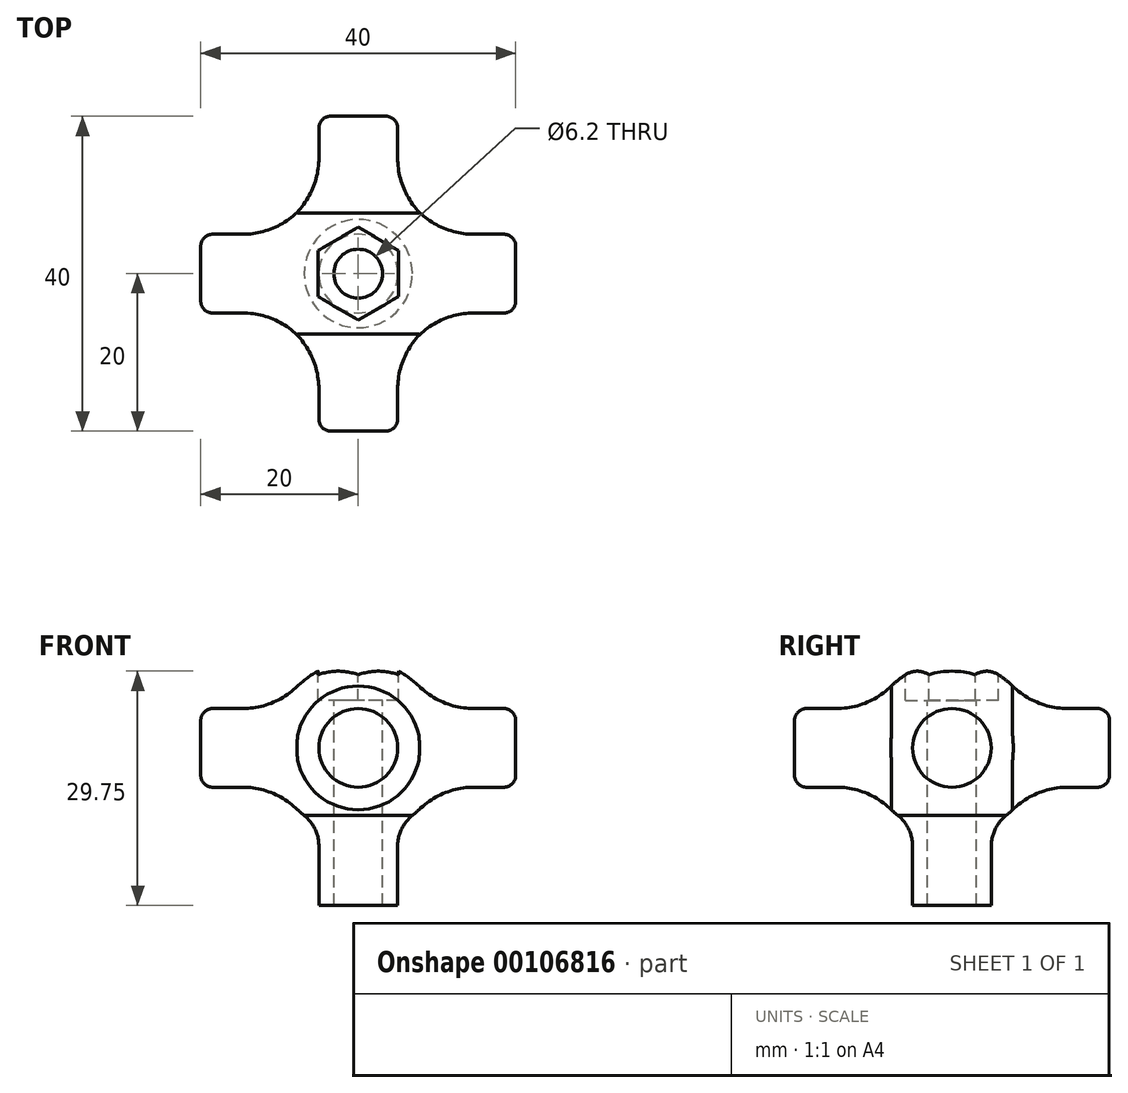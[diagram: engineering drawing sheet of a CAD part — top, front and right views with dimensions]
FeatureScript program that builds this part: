
annotation { "Feature Type Name" : "Feature", "Feature Type Description" : "" }
export const myFeature = defineFeature(function(context is Context, id is Id, definition is map)
    precondition{}
    {
        {
            var Q0;
            Q0=qCreatedBy(makeId("Top.planeOp"),FACE);
            var sketch = newSketch(context, id + "F0", { "sketchPlane" : qUnion([Q0])});
            skCircle(sketch, "E0", {"center": v(0, 0) * mm, "radius": 11 * mm});
            skLineSegment(sketch, "E1", {"start": v(-15.58, 0) * mm, "end": v(16.15, 0) * mm});
            skSolve(sketch);
        }
        {
            var Q0;
            {var subQ0=sQuery(id+"F0.wireOp",EDGE,"E1");var subQ1=sQuery(id+"F0.wireOp",EDGE,"E0");var subQ2=makeQuery(id+"F0.imprint","INTERSECT",VERTEX,{"disambiguationData":[OD(0.0)],"derivedFrom":[subQ1,subQ0]});Q0=makeQuery(id+"F0.imprint","IMPRINT",FACE,{"disambiguationData":[TD([[makeQuery(id+"F0.imprint","IMPRINT",EDGE,{"disambiguationData":[TD([[subQ2,1.0]])],"derivedFrom":subQ1}),1.0]])]});}
            var Q1;
            Q1=sQuery(id+"F0.wireOp",EDGE,"E1");
            revolve(context, id + "F1", {"entities" : qUnion([Q0]), "axis" : qUnion([Q1]), "revolveType" : RevolveType.FULL});
        }
        {
            var Q0;
            Q0=qCreatedBy(makeId("Top.planeOp"),FACE);
            var sketch = newSketch(context, id + "F2", { "sketchPlane" : qUnion([Q0])});
            skCircle(sketch, "E2", {"center": v(0, 0) * mm, "radius": 5 * mm});
            skSolve(sketch);
        }
        {
            var Q0;
            Q0=makeQuery(id+"F2.imprint","IMPRINT",FACE,{"disambiguationData":[TD([[makeQuery(id+"F2.imprint","IMPRINT",EDGE,{"derivedFrom":sQuery(id+"F2.wireOp",EDGE,"E2")}),1.0]])]});
            extrude(context, id + "F3", {"entities" : qUnion([Q0]), "operationType" : NewBodyOperationType.ADD, "oppositeDirection" : true, "depth" : 20 * mm});
        }
        {
            var Q0;
            Q0=qCreatedBy(makeId("Front.planeOp"),FACE);
            var sketch = newSketch(context, id + "F4", { "sketchPlane" : qUnion([Q0])});
            skCircle(sketch, "E3", {"center": v(0, 0) * mm, "radius": 5 * mm});
            skSolve(sketch);
        }
        {
            var Q0;
            Q0=makeQuery(id+"F4.imprint","IMPRINT",FACE,{"disambiguationData":[TD([[makeQuery(id+"F4.imprint","IMPRINT",EDGE,{"derivedFrom":sQuery(id+"F4.wireOp",EDGE,"E3")}),1.0]])]});
            extrude(context, id + "F5", {"entities" : qUnion([Q0]), "operationType" : NewBodyOperationType.ADD, "endBound" : BoundingType.SYMMETRIC, "depth" : 40 * mm});
        }
        {
            var Q0;
            Q0=qCreatedBy(makeId("Right.planeOp"),FACE);
            var sketch = newSketch(context, id + "F6", { "sketchPlane" : qUnion([Q0])});
            skCircle(sketch, "E4", {"center": v(0, 0) * mm, "radius": 5 * mm});
            skSolve(sketch);
        }
        {
            var Q0;
            Q0=makeQuery(id+"F6.imprint","IMPRINT",FACE,{"disambiguationData":[TD([[makeQuery(id+"F6.imprint","IMPRINT",EDGE,{"derivedFrom":sQuery(id+"F6.wireOp",EDGE,"E4")}),1.0]])]});
            extrude(context, id + "F7", {"entities" : qUnion([Q0]), "operationType" : NewBodyOperationType.ADD, "endBound" : BoundingType.SYMMETRIC, "depth" : 40 * mm});
        }
        {
            var Q0;
            Q0=qCreatedBy(makeId("Top.planeOp"),FACE);
            var sketch = newSketch(context, id + "F8", { "sketchPlane" : qUnion([Q0])});
            skLineSegment(sketch, "E5.bottom", {"start": v(-62.48, 40.7) * mm, "end": v(-53.7, 40.7) * mm});
            skLineSegment(sketch, "E5.top", {"start": v(-62.48, 52.9) * mm, "end": v(-53.7, 52.9) * mm});
            skLineSegment(sketch, "E5.left", {"start": v(-62.48, 40.7) * mm, "end": v(-62.48, 52.9) * mm});
            skLineSegment(sketch, "E5.right", {"start": v(-53.7, 40.7) * mm, "end": v(-53.7, 52.9) * mm});
            skSolve(sketch);
        }
        {
            var Q0;
            Q0=makeQuery(id+"F8.imprint","IMPRINT",FACE,{"disambiguationData":[TD([[makeQuery(id+"F8.imprint","IMPRINT",EDGE,{"derivedFrom":sQuery(id+"F8.wireOp",EDGE,"E5.bottom")}),1.0]])]});
            extrude(context, id + "F9", {"entities" : qUnion([Q0]), "depth" : 25 * mm});
        }
        {
            var Q0;
            Q0=makeQuery(id+"F9.opExtrude","CAP_FACE",FACE,{"disambiguationData":[OSD([sQuery(id+"F8.wireOp",EDGE,"E5.bottom"),sQuery(id+"F8.wireOp",EDGE,"E5.top"),sQuery(id+"F8.wireOp",EDGE,"E5.left"),sQuery(id+"F8.wireOp",EDGE,"E5.right")])],"isStart":false});
            var sketch = newSketch(context, id + "F10", { "sketchPlane" : qUnion([Q0])});
            skPoint(sketch, "E6.0", {"position": v(0, 0) * mm});
            skCircle(sketch, "E7.cCircle", {"center": v(0, 0) * mm, "radius": 5.1 * mm, "construction": true});
            skLineSegment(sketch, "E7.0", {"start": v(-5.1, -2.94) * mm, "end": v(-5.1, 2.94) * mm});
            skLineSegment(sketch, "E7.1", {"start": v(-5.1, 2.94) * mm, "end": v(0, 5.89) * mm});
            skLineSegment(sketch, "E7.2", {"start": v(0, 5.89) * mm, "end": v(5.1, 2.94) * mm});
            skLineSegment(sketch, "E7.3", {"start": v(5.1, 2.94) * mm, "end": v(5.1, -2.94) * mm});
            skLineSegment(sketch, "E7.4", {"start": v(5.1, -2.94) * mm, "end": v(0, -5.89) * mm});
            skLineSegment(sketch, "E7.5", {"start": v(0, -5.89) * mm, "end": v(-5.1, -2.94) * mm});
            skPoint(sketch, "E7.0.midPoint", {"position": v(-5.1, 0) * mm});
            skSolve(sketch);
        }
        {
            var Q0;
            Q0=makeQuery(id+"F10.imprint","IMPRINT",FACE,{"disambiguationData":[TD([[makeQuery(id+"F10.imprint","IMPRINT",EDGE,{"derivedFrom":sQuery(id+"F10.wireOp",EDGE,"E7.0")}),-1.0]])]});
            extrude(context, id + "F11", {"entities" : qUnion([Q0]), "operationType" : NewBodyOperationType.REMOVE, "oppositeDirection" : true, "depth" : 19 * mm});
        }
        {
            var Q0;
            Q0=makeQuery(id+"F11.boolean.opBoolean","COPY",FACE,{"derivedFrom":makeQuery(id+"F11.opExtrude","CAP_FACE",FACE,{"disambiguationData":[OSD([sQuery(id+"F10.wireOp",EDGE,"E7.0"),sQuery(id+"F10.wireOp",EDGE,"E7.1"),sQuery(id+"F10.wireOp",EDGE,"E7.2"),sQuery(id+"F10.wireOp",EDGE,"E7.3"),sQuery(id+"F10.wireOp",EDGE,"E7.4"),sQuery(id+"F10.wireOp",EDGE,"E7.5")])],"isStart":false})});
            var sketch = newSketch(context, id + "F12", { "sketchPlane" : qUnion([Q0])});
            skPoint(sketch, "E8.0", {"position": v(0, 0) * mm});
            skCircle(sketch, "E9", {"center": v(0, 0) * mm, "radius": 3.1 * mm});
            skSolve(sketch);
        }
        {
            var Q0;
            Q0=makeQuery(id+"F12.imprint","IMPRINT",FACE,{"disambiguationData":[TD([[makeQuery(id+"F12.imprint","IMPRINT",EDGE,{"derivedFrom":sQuery(id+"F12.wireOp",EDGE,"E9")}),1.0]])]});
            extrude(context, id + "F13", {"entities" : qUnion([Q0]), "operationType" : NewBodyOperationType.REMOVE, "oppositeDirection" : true, "depth" : 43.5 * mm});
        }
        {
            var Q0;
            Q0=makeQuery(id+"F9.opExtrude","SWEPT_BODY",BODY,{"disambiguationData":[OSD([sQuery(id+"F8.wireOp",EDGE,"E5.bottom"),sQuery(id+"F8.wireOp",EDGE,"E5.top"),sQuery(id+"F8.wireOp",EDGE,"E5.left"),sQuery(id+"F8.wireOp",EDGE,"E5.right")])]});
            deleteBodies(context, id + "F14", {"entities" : qUnion([Q0])});
        }
        {
            var Q0;
            Q0=makeQuery(id+"F3.boolean.opBoolean","INTERSECT",EDGE,{"derivedFrom":[makeQuery(id+"F1.opRevolve","SWEPT_FACE",FACE,{"disambiguationData":[OSD([sQuery(id+"F0.wireOp",EDGE,"E0")])]}),makeQuery(id+"F3.opExtrude","SWEPT_FACE",FACE,{"disambiguationData":[OSD([sQuery(id+"F2.wireOp",EDGE,"E2")])]})]});
            fillet(context, id + "F15", {"entities" : qUnion([Q0]), "radius" : 5 * mm, "tangentPropagation" : true, "allowEdgeOverflow" : false});
        }
        {
            var Q0;
            Q0=makeQuery(id+"F7.boolean.opBoolean","INTERSECT",EDGE,{"disambiguationData":[OD(1.0)],"derivedFrom":[makeQuery(id+"F1.opRevolve","SWEPT_FACE",FACE,{"disambiguationData":[OSD([sQuery(id+"F0.wireOp",EDGE,"E0")])]}),makeQuery(id+"F7.opExtrude","SWEPT_FACE",FACE,{"disambiguationData":[OSD([sQuery(id+"F6.wireOp",EDGE,"E4")])]})]});
            var Q1;
            Q1=makeQuery(id+"F5.boolean.opBoolean","INTERSECT",EDGE,{"disambiguationData":[OD(1.0)],"derivedFrom":[makeQuery(id+"F1.opRevolve","SWEPT_FACE",FACE,{"disambiguationData":[OSD([sQuery(id+"F0.wireOp",EDGE,"E0")])]}),makeQuery(id+"F5.opExtrude","SWEPT_FACE",FACE,{"disambiguationData":[OSD([sQuery(id+"F4.wireOp",EDGE,"E3")])]})]});
            var Q2;
            Q2=makeQuery(id+"F5.boolean.opBoolean","INTERSECT",EDGE,{"disambiguationData":[OD(0.0)],"derivedFrom":[makeQuery(id+"F1.opRevolve","SWEPT_FACE",FACE,{"disambiguationData":[OSD([sQuery(id+"F0.wireOp",EDGE,"E0")])]}),makeQuery(id+"F5.opExtrude","SWEPT_FACE",FACE,{"disambiguationData":[OSD([sQuery(id+"F4.wireOp",EDGE,"E3")])]})]});
            var Q3;
            Q3=makeQuery(id+"F7.boolean.opBoolean","INTERSECT",EDGE,{"disambiguationData":[OD(0.0)],"derivedFrom":[makeQuery(id+"F1.opRevolve","SWEPT_FACE",FACE,{"disambiguationData":[OSD([sQuery(id+"F0.wireOp",EDGE,"E0")])]}),makeQuery(id+"F7.opExtrude","SWEPT_FACE",FACE,{"disambiguationData":[OSD([sQuery(id+"F6.wireOp",EDGE,"E4")])]})]});
            fillet(context, id + "F16", {"entities" : qUnion([Q0, Q1, Q2, Q3]), "radius" : 10 * mm, "tangentPropagation" : true, "allowEdgeOverflow" : false});
        }
        {
            var Q0;
            Q0=makeQuery(id+"F5.opExtrude","CAP_EDGE",EDGE,{"disambiguationData":[OSD([sQuery(id+"F4.wireOp",EDGE,"E3")])],"isStart":true});
            fillet(context, id + "F17", {"entities" : qUnion([Q0]), "radius" : 1.5 * mm, "tangentPropagation" : true, "allowEdgeOverflow" : false});
        }
        {
            var Q0;
            Q0=makeQuery(id+"F7.opExtrude","CAP_EDGE",EDGE,{"disambiguationData":[OSD([sQuery(id+"F6.wireOp",EDGE,"E4")])],"isStart":false});
            var Q1;
            Q1=makeQuery(id+"F5.opExtrude","CAP_EDGE",EDGE,{"disambiguationData":[OSD([sQuery(id+"F4.wireOp",EDGE,"E3")])],"isStart":false});
            var Q2;
            Q2=makeQuery(id+"F7.opExtrude","CAP_EDGE",EDGE,{"disambiguationData":[OSD([sQuery(id+"F6.wireOp",EDGE,"E4")])],"isStart":true});
            fillet(context, id + "F18", {"entities" : qUnion([Q0, Q1, Q2]), "radius" : 1.5 * mm, "tangentPropagation" : true, "allowEdgeOverflow" : false});
        }
    });
